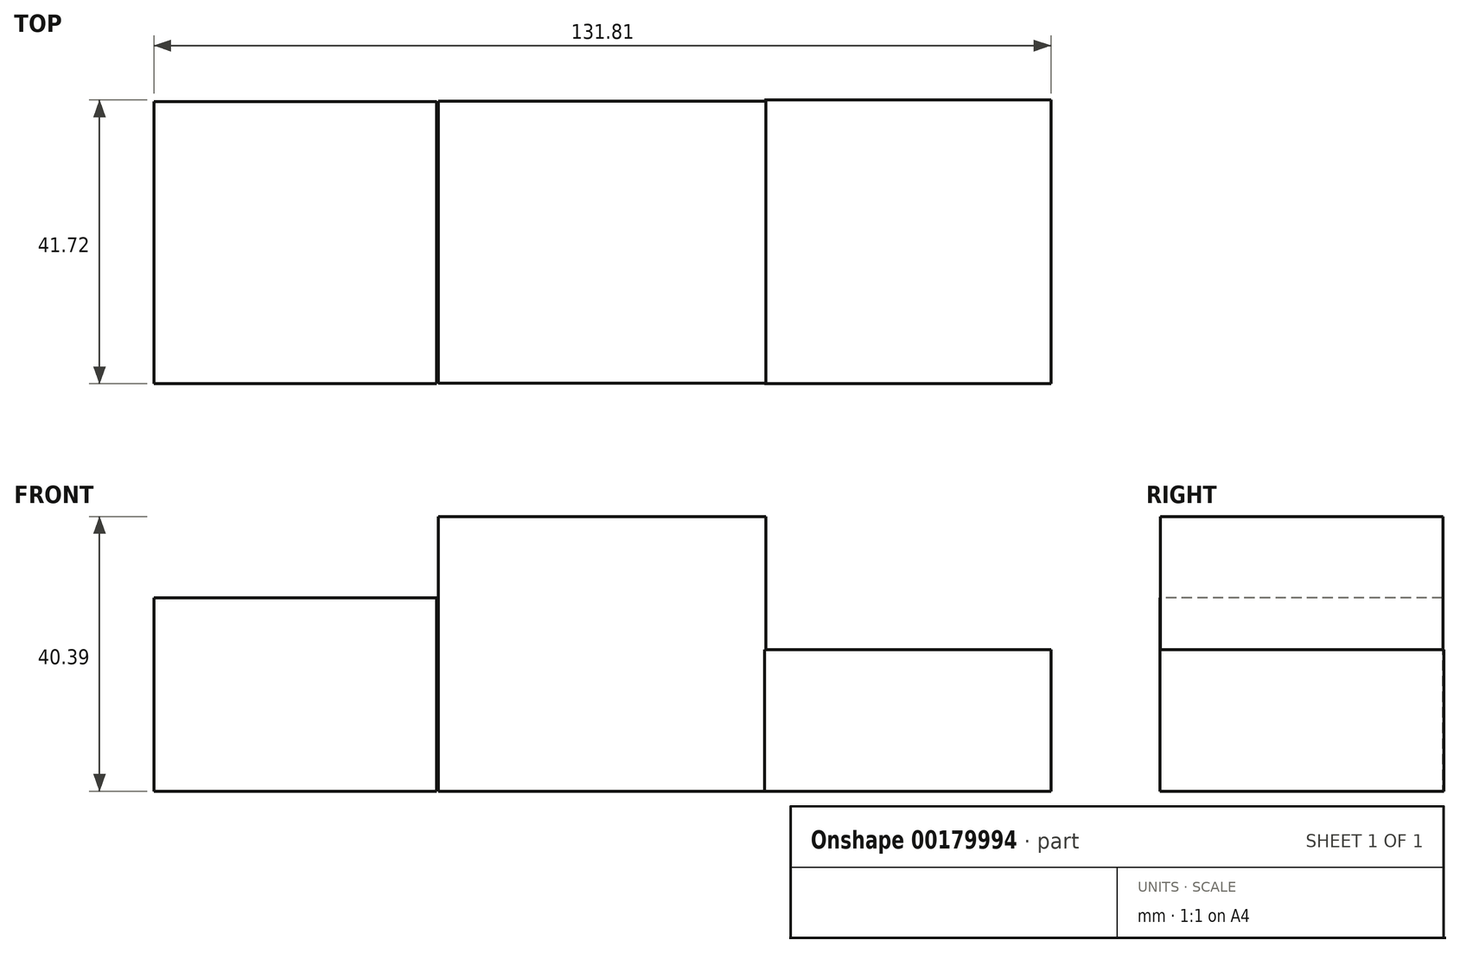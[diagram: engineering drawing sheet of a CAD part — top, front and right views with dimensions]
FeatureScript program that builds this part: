
annotation { "Feature Type Name" : "Feature", "Feature Type Description" : "" }
export const myFeature = defineFeature(function(context is Context, id is Id, definition is map)
    precondition{}
    {
        {
            var Q0;
            Q0=qCreatedBy(makeId("Top.planeOp"),FACE);
            var sketch = newSketch(context, id + "F0", { "sketchPlane" : qUnion([Q0])});
            skLineSegment(sketch, "E0.bottom", {"start": v(-24.8, 20.73) * mm, "end": v(23.34, 20.73) * mm});
            skLineSegment(sketch, "E0.top", {"start": v(-24.8, -20.77) * mm, "end": v(23.34, -20.77) * mm});
            skLineSegment(sketch, "E0.left", {"start": v(-24.8, 20.73) * mm, "end": v(-24.8, -20.77) * mm});
            skLineSegment(sketch, "E0.right", {"start": v(23.34, 20.73) * mm, "end": v(23.34, -20.77) * mm});
            skLineSegment(sketch, "E1.bottom", {"start": v(-24.8, 20.73) * mm, "end": v(-68.13, 20.73) * mm});
            skLineSegment(sketch, "E1.top", {"start": v(-24.8, -20.77) * mm, "end": v(-68.13, -20.77) * mm});
            skLineSegment(sketch, "E1.right", {"start": v(-68.13, 20.73) * mm, "end": v(-68.13, -20.77) * mm});
            skLineSegment(sketch, "E2.bottom", {"start": v(23.34, 20.73) * mm, "end": v(64.27, 20.73) * mm});
            skLineSegment(sketch, "E2.top", {"start": v(23.34, -20.77) * mm, "end": v(64.27, -20.77) * mm});
            skLineSegment(sketch, "E2.right", {"start": v(64.27, 20.73) * mm, "end": v(64.27, -20.77) * mm});
            skSolve(sketch);
        }
        {
            var Q0;
            Q0=makeQuery(id+"F0.imprint","IMPRINT",FACE,{"disambiguationData":[TD([[makeQuery(id+"F0.imprint","IMPRINT",EDGE,{"derivedFrom":sQuery(id+"F0.wireOp",EDGE,"E0.bottom")}),-1.0]])]});
            extrude(context, id + "F1", {"entities" : qUnion([Q0]), "depth" : 40.4 * mm});
        }
        {
            var Q0;
            Q0=qCreatedBy(makeId("Top.planeOp"),FACE);
            var sketch = newSketch(context, id + "F2", { "sketchPlane" : qUnion([Q0])});
            skLineSegment(sketch, "E3.bottom", {"start": v(-25.07, 20.66) * mm, "end": v(-66.6, 20.66) * mm});
            skLineSegment(sketch, "E3.top", {"start": v(-25.07, -20.86) * mm, "end": v(-66.6, -20.86) * mm});
            skLineSegment(sketch, "E3.left", {"start": v(-25.07, 20.66) * mm, "end": v(-25.07, -20.86) * mm});
            skLineSegment(sketch, "E3.right", {"start": v(-66.6, 20.66) * mm, "end": v(-66.6, -20.86) * mm});
            skSolve(sketch);
        }
        {
            var Q0;
            Q0=makeQuery(id+"F2.imprint","IMPRINT",FACE,{"disambiguationData":[TD([[makeQuery(id+"F2.imprint","IMPRINT",EDGE,{"derivedFrom":sQuery(id+"F2.wireOp",EDGE,"E3.bottom")}),1.0]])]});
            extrude(context, id + "F3", {"entities" : qUnion([Q0]), "depth" : 28.45 * mm});
        }
        {
            var Q0;
            Q0=qCreatedBy(makeId("Top.planeOp"),FACE);
            var sketch = newSketch(context, id + "F4", { "sketchPlane" : qUnion([Q0])});
            skLineSegment(sketch, "E4.bottom", {"start": v(23.11, 20.86) * mm, "end": v(65.22, 20.86) * mm});
            skLineSegment(sketch, "E4.top", {"start": v(23.11, -20.86) * mm, "end": v(65.22, -20.86) * mm});
            skLineSegment(sketch, "E4.left", {"start": v(23.11, 20.86) * mm, "end": v(23.11, -20.86) * mm});
            skLineSegment(sketch, "E4.right", {"start": v(65.22, 20.86) * mm, "end": v(65.22, -20.86) * mm});
            skSolve(sketch);
        }
        {
            var Q0;
            Q0=makeQuery(id+"F4.imprint","IMPRINT",FACE,{"disambiguationData":[TD([[makeQuery(id+"F4.imprint","IMPRINT",EDGE,{"derivedFrom":sQuery(id+"F4.wireOp",EDGE,"E4.bottom")}),-1.0]])]});
            extrude(context, id + "F5", {"entities" : qUnion([Q0]), "operationType" : NewBodyOperationType.ADD, "depth" : 20.83 * mm});
        }
    });
